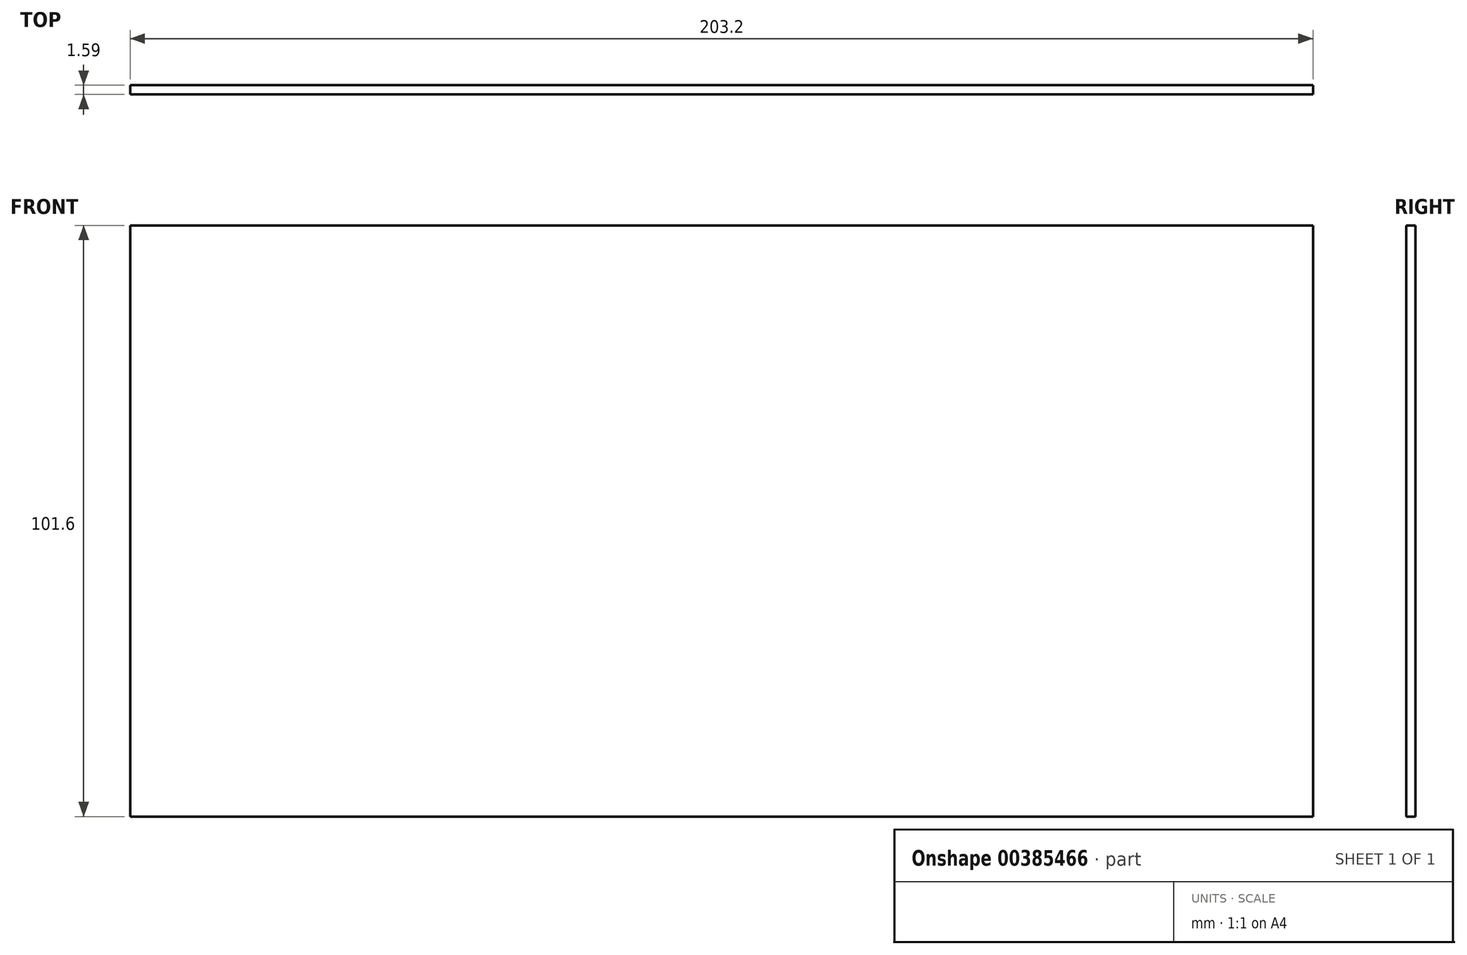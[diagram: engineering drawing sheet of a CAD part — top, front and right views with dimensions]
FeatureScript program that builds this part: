
annotation { "Feature Type Name" : "Feature", "Feature Type Description" : "" }
export const myFeature = defineFeature(function(context is Context, id is Id, definition is map)
    precondition{}
    {
        {
            var Q0;
            Q0=qCreatedBy(makeId("Front.planeOp"),FACE);
            var sketch = newSketch(context, id + "F0", { "sketchPlane" : qUnion([Q0])});
            skLineSegment(sketch, "E0.bottom", {"start": v(101.6, 50.8) * mm, "end": v(-101.6, 50.8) * mm});
            skLineSegment(sketch, "E0.top", {"start": v(101.6, -50.8) * mm, "end": v(-101.6, -50.8) * mm});
            skLineSegment(sketch, "E0.left", {"start": v(101.6, 50.8) * mm, "end": v(101.6, -50.8) * mm});
            skLineSegment(sketch, "E0.right", {"start": v(-101.6, 50.8) * mm, "end": v(-101.6, -50.8) * mm});
            skPoint(sketch, "E0.middle", {"position": v(0, 0) * mm});
            skSolve(sketch);
        }
        {
            var Q0;
            Q0=makeQuery(id+"F0.imprint","IMPRINT",FACE,{"disambiguationData":[TD([[makeQuery(id+"F0.imprint","IMPRINT",EDGE,{"derivedFrom":sQuery(id+"F0.wireOp",EDGE,"E0.bottom")}),1.0]])]});
            extrude(context, id + "F1", {"entities" : qUnion([Q0]), "depth" : 1.59 * mm});
        }
    });
